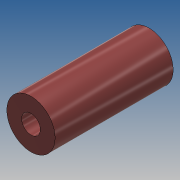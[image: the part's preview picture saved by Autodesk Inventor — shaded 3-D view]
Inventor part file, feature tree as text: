
AUTODESK INVENTOR PART (.ipt)
format: ipt  version: 2017 (Build 210142000, 142)  size: 87,040 bytes
history: native  units: mm
features: other x1, extrude x1, sketch x1
ambient origin geometry x8: Origin, YZ Plane, XZ Plane, XY Plane, X Axis, Y Axis, Z Axis, Center Point
bodies: Body1 (feature_tree)
feature tree (3):
  other  "Sólido1"
  extrude  "Extrusión1"  Depth=22.0mm
  sketch  "Boceto1"  dims[d0=3.5mm d1=9.0mm d2=22.0mm d3=0.0mm]
